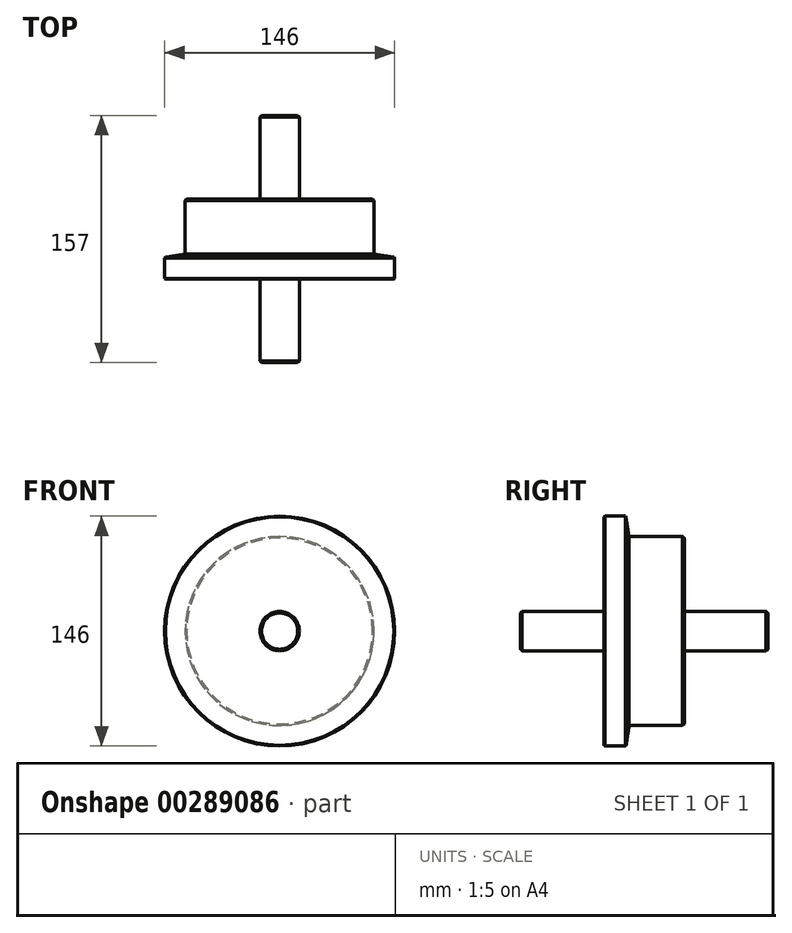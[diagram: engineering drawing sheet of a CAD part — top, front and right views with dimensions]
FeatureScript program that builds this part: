
annotation { "Feature Type Name" : "Feature", "Feature Type Description" : "" }
export const myFeature = defineFeature(function(context is Context, id is Id, definition is map)
    precondition{}
    {
        {
            var Q0;
            Q0=qCreatedBy(makeId("Front.planeOp"),FACE);
            var sketch = newSketch(context, id + "F0", { "sketchPlane" : qUnion([Q0])});
            skCircle(sketch, "E0", {"center": v(0, 0) * mm, "radius": 73 * mm});
            skSolve(sketch);
        }
        {
            var Q0;
            Q0 = qSketchRegion(id + "F0", true);
            extrude(context, id + "F1", {"entities" : qUnion([Q0]), "depth" : 16 * mm});
        }
        {
            var Q0;
            Q0=makeQuery(id+"F1.opExtrude","CAP_FACE",FACE,{"disambiguationData":[OSD([sQuery(id+"F0.wireOp",EDGE,"E0")])],"isStart":true});
            var sketch = newSketch(context, id + "F2", { "sketchPlane" : qUnion([Q0])});
            skCircle(sketch, "E1", {"center": v(0, 0) * mm, "radius": 60 * mm});
            skSolve(sketch);
        }
        {
            var Q0;
            Q0 = qSketchRegion(id + "F2", true);
            extrude(context, id + "F3", {"entities" : qUnion([Q0]), "operationType" : NewBodyOperationType.ADD, "depth" : 35 * mm});
        }
        {
            var Q0;
            Q0=makeQuery(id+"F3.opExtrude","CAP_FACE",FACE,{"disambiguationData":[OSD([sQuery(id+"F2.wireOp",EDGE,"E1")])],"isStart":false});
            var sketch = newSketch(context, id + "F4", { "sketchPlane" : qUnion([Q0])});
            skCircle(sketch, "E2", {"center": v(0, 0) * mm, "radius": 12.5 * mm});
            skSolve(sketch);
        }
        {
            var Q0;
            Q0 = qSketchRegion(id + "F4", true);
            extrude(context, id + "F5", {"entities" : qUnion([Q0]), "operationType" : NewBodyOperationType.ADD, "depth" : 53 * mm});
        }
        {
            var Q0;
            Q0=makeQuery(id+"F1.opExtrude","CAP_FACE",FACE,{"disambiguationData":[OSD([sQuery(id+"F0.wireOp",EDGE,"E0")])],"isStart":false});
            var sketch = newSketch(context, id + "F6", { "sketchPlane" : qUnion([Q0])});
            skCircle(sketch, "E3", {"center": v(0, 0) * mm, "radius": 12.5 * mm});
            skSolve(sketch);
        }
        {
            var Q0;
            Q0 = qSketchRegion(id + "F6", true);
            extrude(context, id + "F7", {"entities" : qUnion([Q0]), "operationType" : NewBodyOperationType.ADD, "depth" : 53 * mm});
        }
        {
            var Q0;
            Q0=makeQuery(id+"F1.opExtrude","CAP_EDGE",EDGE,{"disambiguationData":[OSD([sQuery(id+"F0.wireOp",EDGE,"E0")])],"isStart":true});
            chamfer(context, id + "F8", {"entities" : qUnion([Q0]), "chamferType" : ChamferType.TWO_OFFSETS, "width1" : 2 * mm, "oppositeDirection" : false, "width2" : (26 / 2) * mm, "tangentPropagation" : true});
        }
        {
            var Q0;
            {var subQ0=sQuery(id+"F0.wireOp",EDGE,"E0");Q0=makeQuery(id+"F8.opChamfer","BLEND_EDGE",EDGE,{"blendedFrom":[makeQuery(id+"F1.opExtrude","CAP_EDGE",EDGE,{"disambiguationData":[OSD([subQ0])],"isStart":true}),makeQuery(id+"F1.opExtrude","SWEPT_FACE",FACE,{"disambiguationData":[OSD([subQ0])]})],"blendedInto":[makeQuery(id+"F1.opExtrude","SWEPT_FACE",FACE,{"disambiguationData":[OSD([subQ0])]})]});}
            var Q1;
            Q1=makeQuery(id+"F1.opExtrude","CAP_EDGE",EDGE,{"disambiguationData":[OSD([sQuery(id+"F0.wireOp",EDGE,"E0")])],"isStart":false});
            chamfer(context, id + "F9", {"entities" : qUnion([Q0, Q1]), "width" : .5 * mm, "tangentPropagation" : true});
        }
        {
            var Q0;
            Q0=makeQuery(id+"F3.opExtrude","CAP_EDGE",EDGE,{"disambiguationData":[OSD([sQuery(id+"F2.wireOp",EDGE,"E1")])],"isStart":false});
            var Q1;
            Q1=makeQuery(id+"F5.opExtrude","CAP_EDGE",EDGE,{"disambiguationData":[OSD([sQuery(id+"F4.wireOp",EDGE,"E2")])],"isStart":false});
            var Q2;
            Q2=makeQuery(id+"F7.opExtrude","CAP_EDGE",EDGE,{"disambiguationData":[OSD([sQuery(id+"F6.wireOp",EDGE,"E3")])],"isStart":false});
            chamfer(context, id + "F10", {"entities" : qUnion([Q0, Q1, Q2]), "width" : 1 * mm, "tangentPropagation" : true});
        }
    });
